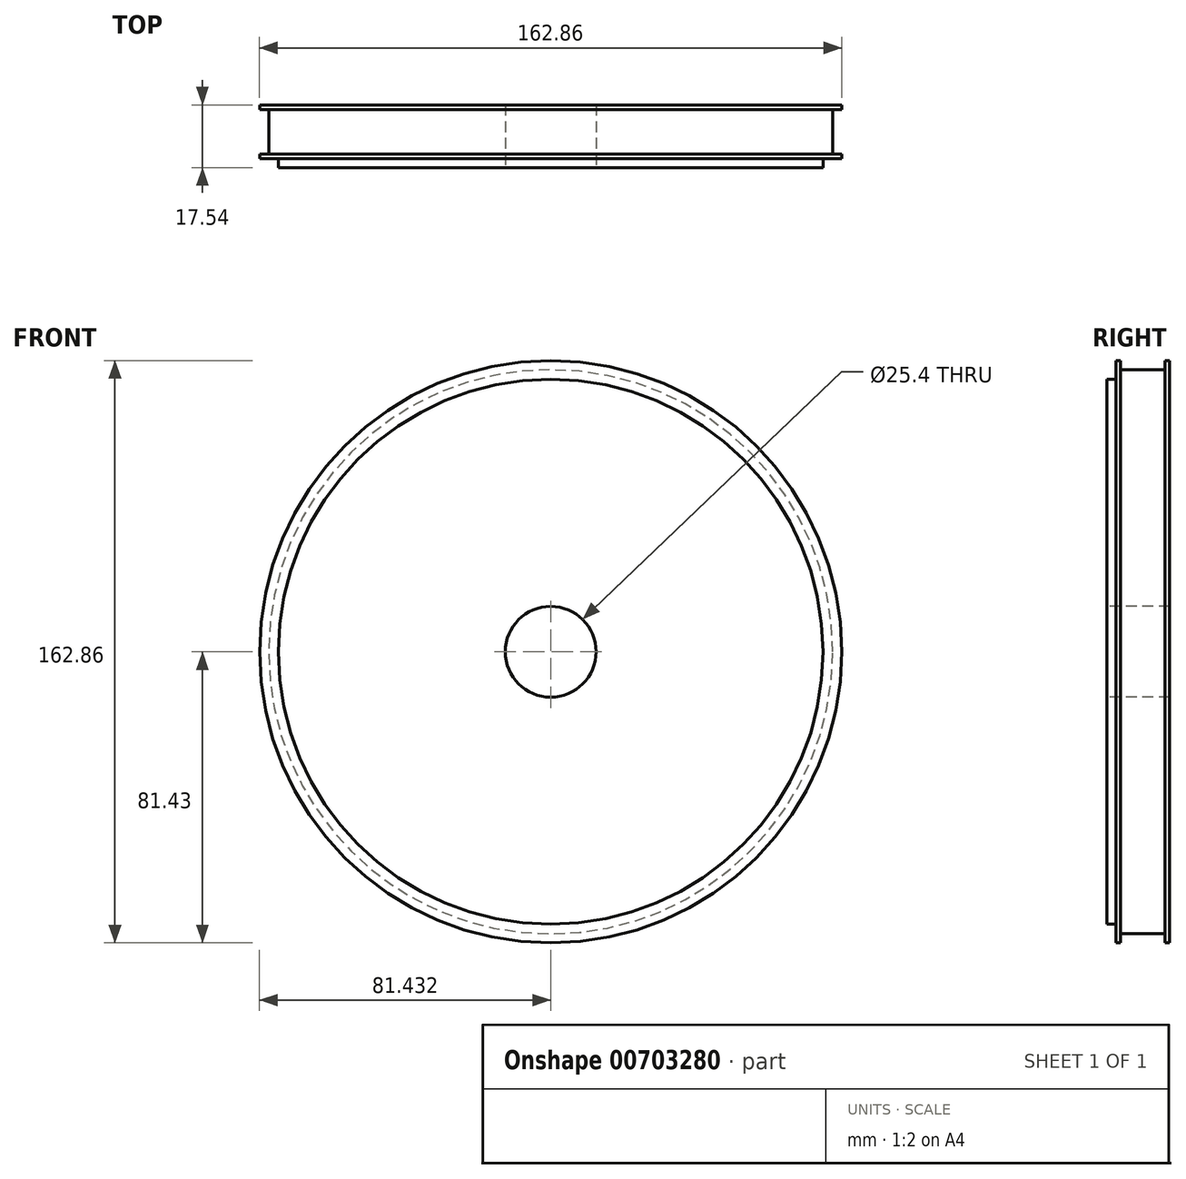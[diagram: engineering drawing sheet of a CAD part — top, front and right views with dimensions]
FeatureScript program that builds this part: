
annotation { "Feature Type Name" : "Feature", "Feature Type Description" : "" }
export const myFeature = defineFeature(function(context is Context, id is Id, definition is map)
    precondition{}
    {
        {
            var Q0;
            Q0=qCreatedBy(makeId("Top.planeOp"),FACE);
            var sketch = newSketch(context, id + "F0", { "sketchPlane" : qUnion([Q0])});
            skLineSegment(sketch, "E0.bottom", {"start": v(-128.17, -3.24) * mm, "end": v(-125.63, -3.24) * mm});
            skLineSegment(sketch, "E0.top", {"start": v(-128.17, -15.7) * mm, "end": v(-125.63, -15.7) * mm});
            skLineSegment(sketch, "E0.right", {"start": v(-125.63, -3.24) * mm, "end": v(-125.63, -15.7) * mm});
            skLineSegment(sketch, "E1.top", {"start": v(-122.92, -19.51) * mm, "end": v(-59.44, -19.51) * mm});
            skLineSegment(sketch, "E1.left", {"start": v(-122.92, -16.97) * mm, "end": v(-122.92, -19.51) * mm});
            skLineSegment(sketch, "E1.right", {"start": v(-59.44, -16.97) * mm, "end": v(-59.44, -19.51) * mm});
            skLineSegment(sketch, "E2", {"start": v(-128.17, -15.7) * mm, "end": v(-128.17, -16.97) * mm});
            skLineSegment(sketch, "E3", {"start": v(-128.17, -1.97) * mm, "end": v(-128.17, -3.24) * mm});
            skLineSegment(sketch, "E4", {"start": v(-122.92, -16.97) * mm, "end": v(-128.17, -16.97) * mm});
            skLineSegment(sketch, "E5", {"start": v(-46.74, -16.97) * mm, "end": v(-46.74, -1.97) * mm});
            skLineSegment(sketch, "E6", {"start": v(-122.92, -16.97) * mm, "end": v(-46.74, -16.97) * mm});
            skLineSegment(sketch, "E7", {"start": v(-46.74, -1.97) * mm, "end": v(-128.17, -1.97) * mm});
            skLineSegment(sketch, "E8", {"start": v(-59.44, -16.97) * mm, "end": v(-59.44, -1.97) * mm});
            skSolve(sketch);
        }
        {
            var Q0;
            Q0=makeQuery(id+"F0.imprint","IMPRINT",FACE,{"disambiguationData":[TD([[makeQuery(id+"F0.imprint","IMPRINT",EDGE,{"derivedFrom":sQuery(id+"F0.wireOp",EDGE,"E0.bottom")}),1.0]])]});
            var Q1;
            {var subQ0=sQuery(id+"F0.wireOp",EDGE,"E1.top");Q1=makeQuery(id+"F0.imprint","IMPRINT",FACE,{"disambiguationData":[TD([[makeQuery(id+"F0.imprint","IMPRINT",EDGE,{"derivedFrom":subQ0}),1.0]])]});}
            var Q2;
            Q2=sQuery(id+"F0.wireOp",EDGE,"E5");
            revolve(context, id + "F1", {"surfaceOperationType" : NewSurfaceOperationType.NEW, "entities" : qUnion([Q0, Q1]), "axis" : qUnion([Q2]), "revolveType" : RevolveType.FULL});
        }
    });
